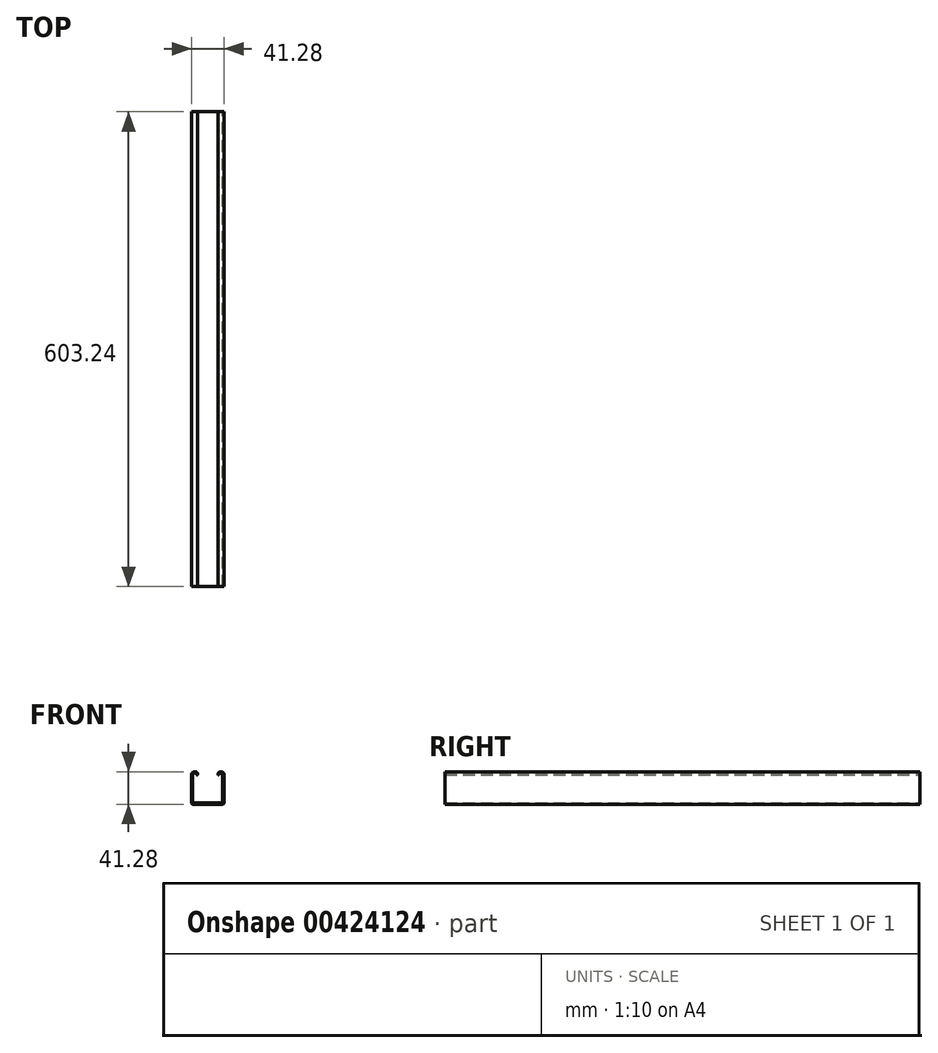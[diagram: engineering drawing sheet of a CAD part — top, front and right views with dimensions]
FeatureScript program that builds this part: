
annotation { "Feature Type Name" : "Feature", "Feature Type Description" : "" }
export const myFeature = defineFeature(function(context is Context, id is Id, definition is map)
    precondition{}
    {
        {
            var Q0;
            Q0=qCreatedBy(makeId("Front.planeOp"),FACE);
            var sketch = newSketch(context, id + "F0", { "sketchPlane" : qUnion([Q0])});
            skLineSegment(sketch, "E0.bottom", {"start": v(0, 0) * mm, "end": v(41.28, 0) * mm});
            skLineSegment(sketch, "E0.left", {"start": v(0, 0) * mm, "end": v(0, 37.31) * mm});
            skLineSegment(sketch, "E0.right", {"start": v(41.28, 0) * mm, "end": v(41.27, 37.31) * mm});
            skLineSegment(sketch, "E1.0", {"start": v(1.59, 1.59) * mm, "end": v(1.59, 37.31) * mm});
            skLineSegment(sketch, "E2.0", {"start": v(1.59, 1.59) * mm, "end": v(39.69, 1.59) * mm});
            skArc(sketch, "E3", {"start": v(7.92, 37.31) * mm, "mid": v(3.96, 41.28) * mm, "end": v(0, 37.31) * mm});
            skArc(sketch, "E4", {"start": v(6.34, 37.31) * mm, "mid": v(3.96, 39.69) * mm, "end": v(1.59, 37.31) * mm});
            skLineSegment(sketch, "E5.trimOffspring", {"start": v(6.34, 37.31) * mm, "end": v(7.92, 37.31) * mm});
            skLineSegment(sketch, "E6.MirrorCS", {"start": v(39.69, 1.59) * mm, "end": v(39.69, 37.31) * mm});
            skArc(sketch, "E7.MirrorCS", {"start": v(34.94, 37.31) * mm, "mid": v(37.31, 39.69) * mm, "end": v(39.69, 37.31) * mm});
            skLineSegment(sketch, "E8.MirrorCS", {"start": v(34.94, 37.31) * mm, "end": v(33.35, 37.31) * mm});
            skArc(sketch, "E9.MirrorCS", {"start": v(33.35, 37.31) * mm, "mid": v(37.31, 41.28) * mm, "end": v(41.28, 37.31) * mm});
            skPoint(sketch, "E10.start.orphan", {"position": v(20.64, 0) * mm});
            skSolve(sketch);
        }
        {
            var Q0;
            Q0 = qSketchRegion(id + "F0", true);
            extrude(context, id + "F1", {"entities" : qUnion([Q0]), "endBound" : BoundingType.SYMMETRIC, "depth" : 603.25 * mm});
        }
        {
            var Q0;
            Q0=makeQuery(id+"F1.opExtrude","SWEPT_EDGE",EDGE,{"disambiguationData":[OSD([sQuery(id+"F0.wireOp",EDGE,"E0.bottom"),sQuery(id+"F0.wireOp",EDGE,"E0.left")])]});
            var Q1;
            Q1=makeQuery(id+"F1.opExtrude","SWEPT_EDGE",EDGE,{"disambiguationData":[OSD([sQuery(id+"F0.wireOp",EDGE,"E0.bottom"),sQuery(id+"F0.wireOp",EDGE,"E0.right")])]});
            var Q2;
            Q2=makeQuery(id+"F1.opExtrude","SWEPT_EDGE",EDGE,{"disambiguationData":[OSD([sQuery(id+"F0.wireOp",EDGE,"E2.0"),sQuery(id+"F0.wireOp",EDGE,"E6.MirrorCS")])]});
            var Q3;
            Q3=makeQuery(id+"F1.opExtrude","SWEPT_EDGE",EDGE,{"disambiguationData":[OSD([sQuery(id+"F0.wireOp",EDGE,"E1.0"),sQuery(id+"F0.wireOp",EDGE,"E2.0")])]});
            fillet(context, id + "F2", {"entities" : qUnion([Q0, Q1, Q2, Q3]), "radius" : 1.59 * mm, "tangentPropagation" : true, "allowEdgeOverflow" : false});
        }
        {
            var Q0;
            Q0=makeQuery(id+"F1.opExtrude","SWEPT_EDGE",EDGE,{"disambiguationData":[OSD([sQuery(id+"F0.wireOp",EDGE,"E4"),sQuery(id+"F0.wireOp",EDGE,"E5.trimOffspring")])]});
            var Q1;
            Q1=makeQuery(id+"F1.opExtrude","SWEPT_EDGE",EDGE,{"disambiguationData":[OSD([sQuery(id+"F0.wireOp",EDGE,"E3"),sQuery(id+"F0.wireOp",EDGE,"E5.trimOffspring")])]});
            var Q2;
            Q2=makeQuery(id+"F1.opExtrude","SWEPT_EDGE",EDGE,{"disambiguationData":[OSD([sQuery(id+"F0.wireOp",EDGE,"E8.MirrorCS"),sQuery(id+"F0.wireOp",EDGE,"E9.MirrorCS")])]});
            var Q3;
            Q3=makeQuery(id+"F1.opExtrude","SWEPT_EDGE",EDGE,{"disambiguationData":[OSD([sQuery(id+"F0.wireOp",EDGE,"E7.MirrorCS"),sQuery(id+"F0.wireOp",EDGE,"E8.MirrorCS")])]});
            fillet(context, id + "F3", {"entities" : qUnion([Q0, Q1, Q2, Q3]), "radius" : 0.64 * mm, "tangentPropagation" : true, "allowEdgeOverflow" : false});
        }
    });
